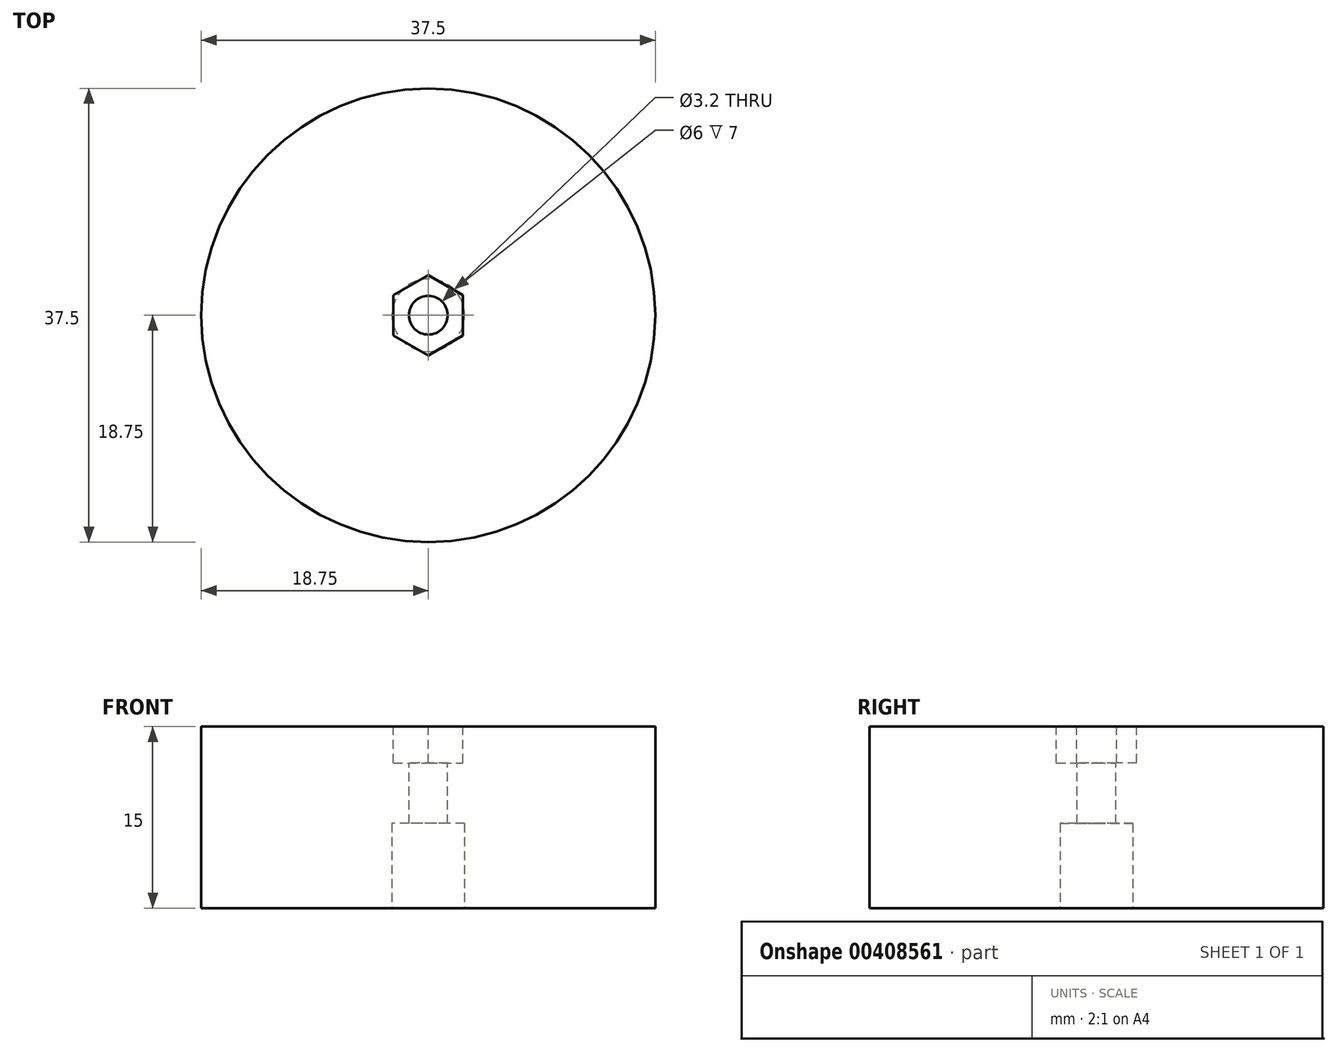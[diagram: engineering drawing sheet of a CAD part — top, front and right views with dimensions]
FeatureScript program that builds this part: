
annotation { "Feature Type Name" : "Feature", "Feature Type Description" : "" }
export const myFeature = defineFeature(function(context is Context, id is Id, definition is map)
    precondition{}
    {
        {
            var Q0;
            Q0=qCreatedBy(makeId("Top.planeOp"),FACE);
            var sketch = newSketch(context, id + "F0", { "sketchPlane" : qUnion([Q0])});
            skCircle(sketch, "E0", {"center": v(0, 0) * mm, "radius": 18.75 * mm});
            skSolve(sketch);
        }
        {
            var Q0;
            Q0 = qSketchRegion(id + "F0", true);
            extrude(context, id + "F1", {"entities" : qUnion([Q0]), "depth" : 15 * mm});
        }
        {
            var Q0;
            Q0=makeQuery(id+"F1.opExtrude","CAP_FACE",FACE,{"disambiguationData":[OSD([sQuery(id+"F0.wireOp",EDGE,"E0")])],"isStart":false});
            var sketch = newSketch(context, id + "F2", { "sketchPlane" : qUnion([Q0])});
            skCircle(sketch, "E1.cCircle", {"center": v(0, 0) * mm, "radius": 2.88 * mm, "construction": true});
            skLineSegment(sketch, "E1.0", {"start": v(2.88, 1.66) * mm, "end": v(2.88, -1.66) * mm});
            skLineSegment(sketch, "E1.1", {"start": v(2.88, -1.66) * mm, "end": v(0, -3.32) * mm});
            skLineSegment(sketch, "E1.2", {"start": v(0, -3.32) * mm, "end": v(-2.88, -1.66) * mm});
            skLineSegment(sketch, "E1.3", {"start": v(-2.87, -1.66) * mm, "end": v(-2.88, 1.66) * mm});
            skLineSegment(sketch, "E1.4", {"start": v(-2.88, 1.66) * mm, "end": v(0, 3.32) * mm});
            skLineSegment(sketch, "E1.5", {"start": v(0, 3.32) * mm, "end": v(2.87, 1.66) * mm});
            skPoint(sketch, "E1.0.midPoint", {"position": v(2.88, 0) * mm});
            skSolve(sketch);
        }
        {
            var Q0;
            Q0 = qSketchRegion(id + "F2", true);
            extrude(context, id + "F3", {"entities" : qUnion([Q0]), "operationType" : NewBodyOperationType.REMOVE, "oppositeDirection" : true, "depth" : 3 * mm});
        }
        {
            var Q0;
            Q0=makeQuery(id+"F3.boolean.opBoolean","COPY",FACE,{"derivedFrom":makeQuery(id+"F3.opExtrude","CAP_FACE",FACE,{"disambiguationData":[OSD([sQuery(id+"F2.wireOp",EDGE,"E1.0"),sQuery(id+"F2.wireOp",EDGE,"E1.1"),sQuery(id+"F2.wireOp",EDGE,"E1.2"),sQuery(id+"F2.wireOp",EDGE,"E1.3"),sQuery(id+"F2.wireOp",EDGE,"E1.4"),sQuery(id+"F2.wireOp",EDGE,"E1.5")])],"isStart":false})});
            var sketch = newSketch(context, id + "F4", { "sketchPlane" : qUnion([Q0])});
            skCircle(sketch, "E2", {"center": v(0, 0) * mm, "radius": 1.6 * mm});
            skSolve(sketch);
        }
        {
            var Q0;
            Q0 = qSketchRegion(id + "F4", true);
            extrude(context, id + "F5", {"entities" : qUnion([Q0]), "operationType" : NewBodyOperationType.REMOVE, "oppositeDirection" : true, "depth" : 25 * mm});
        }
        {
            var Q0;
            Q0=makeQuery(id+"F0.imprint","IMPRINT",FACE,{"disambiguationData":[TD([[makeQuery(id+"F0.imprint","IMPRINT",EDGE,{"derivedFrom":sQuery(id+"F0.wireOp",EDGE,"E0")}),1.0]])]});
            var sketch = newSketch(context, id + "F6", { "sketchPlane" : qUnion([Q0])});
            skCircle(sketch, "E3", {"center": v(0, 0) * mm, "radius": 3 * mm});
            skSolve(sketch);
        }
        {
            var Q0;
            Q0 = qSketchRegion(id + "F6", true);
            extrude(context, id + "F7", {"entities" : qUnion([Q0]), "operationType" : NewBodyOperationType.REMOVE, "depth" : 7 * mm});
        }
    });
